# Revit family: Faucet-Lavatory-KOHLER-MEMOIRS-K-454T_2
name_source: partatom
category: Plumbing Fixtures
revit_build: Autodesk Revit 2017 (Build: 20160225_1515(x64)
units: mm (PartAtom-declared; Revit-internal decimal feet)

## family parameters
Cut with Voids When Loaded = No
Host = Face
OmniClass Number = 23.31.11.00
OmniClass Title = Faucets
Part Type = Normal
Room Calculation Point = No
Round Connector Dimension = Use Diameter
Shared = No

## types (6) — shared parameters
ADA Compliant = No
Assembly Code = D2010
CW Connection = Yes
Cold Water Inlet = Cold Water Inlet
Date Modified = 06/11/2020
Default Elevation = 36"
Description = MEMOIRS WIDESPREAD LAVATORY FAUCET
Drain Included = Yes
Flow Rate = 0 GPM
HW Connection = Yes
Height = 3 5/16"
Hot Water Inlet = Hot Water Inlet
Length = 4 3/4"
Manufacturer = KOHLER Co.
Master Format 2014 = 22 41 39
Master Format 2014 Name = Residential Faucets, Supplies, and Trim
Material = Premium Metal Construction
Pressure = 0.00 psi
Product Documentation Link = http://files.kohler.com.cn
Product Name = MEMOIRS
Product Page URL = http://www.kohler.com.cn
Spout Reach = 4 3/4"
URL = http://www.kohler.com.cn
Vent Connection = No
Waste Connection = No
Waste Water Outlet = Waste Water Outlet
WaterSense Certified = No

## per-type parameters (varying)
| type | Cross Handle | Finish | Handle Clearance | Lever Handle | Model | Type |
| Cross Handle, CP-Polished Chrome | Yes | Kohler-Metal-CP-Polished_Chrome | 1 5/16" | No | K-454T-3S-CP | 1 |
| Lever Handle, CP-Polished Chrome | No | Kohler-Metal-CP-Polished_Chrome | 2 1/2" | Yes | K-454T-4V-CP | 2 |
| Lever Handle, AF-Flange Gold | No | Kohler-Metal-AF-Flange_Gold | 2 1/2" | Yes | K-454T-4V-AF | 3 |
| Lever Handle, BN-Roman Silver | No | Kohler-Metal-BN-Roman_Silver | 2 1/2" | Yes | K-454T-4V-BN | 4 |
| Lever Handle, SN-Champagne Gold | No | Kohler-Metal-SN-Champagne_Gold | 2 1/2" | Yes | K-454T-4V-SN | 5 |
| Lever Handle, RGD-Rose Gold | No | Kohler-Metal-RGD-Rose_Gold | 2 1/2" | Yes | K-454T-4V-RGD | 6 |

## geometry (parser evidence)
native form markers: Sweep x8
no freeform markers — native parametric forms only
